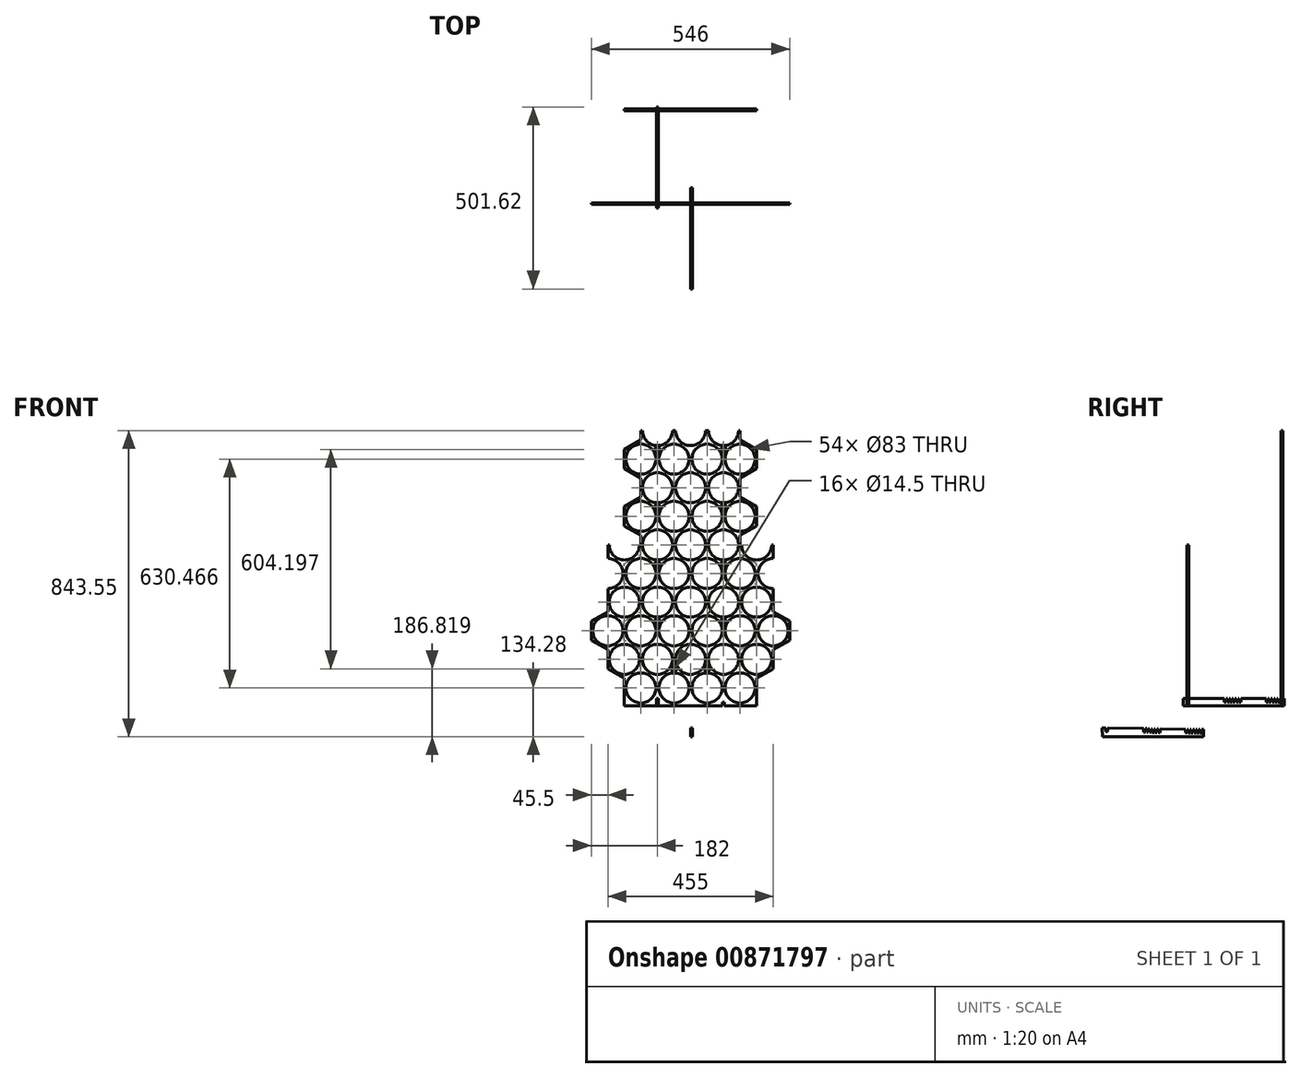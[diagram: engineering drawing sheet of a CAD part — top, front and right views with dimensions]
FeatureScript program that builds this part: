
annotation { "Feature Type Name" : "Feature", "Feature Type Description" : "" }
export const myFeature = defineFeature(function(context is Context, id is Id, definition is map)
    precondition{}
    {
        {
            var Q0;
            Q0=qCreatedBy(makeId("Front.planeOp"),FACE);
            var sketch = newSketch(context, id + "F0", { "sketchPlane" : qUnion([Q0])});
            skLineSegment(sketch, "E0", {"start": v(0, 0) * mm, "end": v(-88.5, 0) * mm});
            skCircle(sketch, "E1", {"center": v(-45.5, 49.5) * mm, "radius": 41.5 * mm});
            skCircle(sketch, "E2", {"center": v(-136.5, 49.5) * mm, "radius": 41.5 * mm});
            skCircle(sketch, "E3", {"center": v(-91, 128.3) * mm, "radius": 41.5 * mm});
            skCircle(sketch, "E4", {"center": v(-182, 128.3) * mm, "radius": 41.5 * mm});
            skArc(sketch, "E5", {"start": v(0, 169.8) * mm, "mid": v(-41.5, 128.3) * mm, "end": v(0, 86.8) * mm});
            skLineSegment(sketch, "E6.trimOffspring", {"start": v(0, 86.8) * mm, "end": v(0, 0) * mm});
            skLineSegment(sketch, "E7", {"start": v(-182, 0) * mm, "end": v(-182, 75.77) * mm});
            skLineSegment(sketch, "E8", {"start": v(-182, 75.77) * mm, "end": v(-227.5, 102.04) * mm});
            skLineSegment(sketch, "E9", {"start": v(-227.5, 102.04) * mm, "end": v(-227.5, 154.58) * mm});
            skLineSegment(sketch, "E10", {"start": v(-227.5, 154.58) * mm, "end": v(-182, 180.85) * mm});
            skLineSegment(sketch, "E11", {"start": v(-182, 180.85) * mm, "end": v(-136.5, 154.58) * mm});
            skLineSegment(sketch, "E12", {"start": v(-136.5, 154.58) * mm, "end": v(-91, 180.85) * mm});
            skLineSegment(sketch, "E13", {"start": v(-91, 180.85) * mm, "end": v(-45.5, 154.58) * mm});
            skLineSegment(sketch, "E14", {"start": v(-45.5, 154.58) * mm, "end": v(0, 180.85) * mm});
            skLineSegment(sketch, "E15", {"start": v(0, 180.85) * mm, "end": v(0, 169.8) * mm});
            skLineSegment(sketch, "E16", {"start": v(-93.5, 0) * mm, "end": v(-93.5, 10) * mm});
            skLineSegment(sketch, "E17", {"start": v(-93.5, 10) * mm, "end": v(-88.5, 10) * mm});
            skLineSegment(sketch, "E18", {"start": v(-88.5, 10) * mm, "end": v(-88.5, 0) * mm});
            skLineSegment(sketch, "E19", {"start": v(-91, 69.8) * mm, "end": v(-91, 32.96) * mm, "construction": true});
            skLineSegment(sketch, "E20.trimOffspring", {"start": v(-93.5, 0) * mm, "end": v(-182, 0) * mm});
            skSolve(sketch);
        }
        {
            var Q0;
            Q0=makeQuery(id+"F0.imprint","IMPRINT",FACE,{"disambiguationData":[TD([[makeQuery(id+"F0.imprint","IMPRINT",EDGE,{"derivedFrom":sQuery(id+"F0.wireOp",EDGE,"E0")}),-1.0]])]});
            extrude(context, id + "F1", {"entities" : qUnion([Q0]), "depth" : 5 * mm, "offsetDistance" : 25 * mm});
        }
        {
            var Q0;
            Q0=qCreatedBy(makeId("Front.planeOp"),FACE);
            var sketch = newSketch(context, id + "F2", { "sketchPlane" : qUnion([Q0])});
            skCircle(sketch, "E21", {"center": v(-136.5, 207.12) * mm, "radius": 41.5 * mm});
            skCircle(sketch, "E22", {"center": v(-45.5, 207.12) * mm, "radius": 41.5 * mm});
            skCircle(sketch, "E23", {"center": v(-227.5, 207.12) * mm, "radius": 41.5 * mm});
            skLineSegment(sketch, "E24.0", {"start": v(-45.5, 154.58) * mm, "end": v(0, 180.85) * mm});
            skLineSegment(sketch, "E24.1", {"start": v(-91, 180.85) * mm, "end": v(-45.5, 154.58) * mm});
            skLineSegment(sketch, "E24.2", {"start": v(-136.5, 154.58) * mm, "end": v(-91, 180.85) * mm});
            skLineSegment(sketch, "E24.3", {"start": v(-182, 180.85) * mm, "end": v(-136.5, 154.58) * mm});
            skLineSegment(sketch, "E24.4", {"start": v(-227.5, 154.58) * mm, "end": v(-182, 180.85) * mm});
            skLineSegment(sketch, "E25", {"start": v(-227.5, 154.58) * mm, "end": v(-273, 180.85) * mm});
            skLineSegment(sketch, "E26", {"start": v(-273, 180.85) * mm, "end": v(-273, 233.39) * mm});
            skLineSegment(sketch, "E27", {"start": v(-227.5, 312.2) * mm, "end": v(-182, 338.46) * mm});
            skLineSegment(sketch, "E28", {"start": v(-182, 338.46) * mm, "end": v(-136.5, 312.2) * mm});
            skLineSegment(sketch, "E29", {"start": v(-136.5, 312.2) * mm, "end": v(-91, 338.46) * mm});
            skLineSegment(sketch, "E30", {"start": v(-91, 338.46) * mm, "end": v(-45.5, 312.2) * mm});
            skLineSegment(sketch, "E31", {"start": v(-45.5, 312.2) * mm, "end": v(0, 338.46) * mm});
            skCircle(sketch, "E32", {"center": v(-182, 285.92) * mm, "radius": 41.5 * mm});
            skCircle(sketch, "E33", {"center": v(-91, 285.92) * mm, "radius": 41.5 * mm});
            skArc(sketch, "E34", {"start": v(0, 327.42) * mm, "mid": v(-41.5, 285.92) * mm, "end": v(0, 244.42) * mm});
            skLineSegment(sketch, "E35", {"start": v(0, 338.46) * mm, "end": v(0, 180.85) * mm});
            skLineSegment(sketch, "E36", {"start": v(-227.5, 312.2) * mm, "end": v(-227.5, 259.66) * mm});
            skLineSegment(sketch, "E37", {"start": v(-227.5, 259.66) * mm, "end": v(-273, 233.39) * mm});
            skSolve(sketch);
        }
        {
            var Q0;
            Q0=makeQuery(id+"F2.imprint","IMPRINT",FACE,{"disambiguationData":[TD([[makeQuery(id+"F2.imprint","IMPRINT",EDGE,{"derivedFrom":sQuery(id+"F2.wireOp",EDGE,"E21")}),-1.0]])]});
            extrude(context, id + "F3", {"entities" : qUnion([Q0]), "depth" : 5 * mm, "offsetDistance" : 25 * mm});
        }
        {
            var Q0;
            Q0=qCreatedBy(makeId("Front.planeOp"),FACE);
            var sketch = newSketch(context, id + "F4", { "sketchPlane" : qUnion([Q0])});
            skCircle(sketch, "E38", {"center": v(-136.5, 364.73) * mm, "radius": 41.5 * mm});
            skCircle(sketch, "E39", {"center": v(-45.5, 364.73) * mm, "radius": 41.5 * mm});
            skArc(sketch, "E40", {"start": v(-227.5, 323.23) * mm, "mid": v(-186, 364.73) * mm, "end": v(-227.5, 406.23) * mm});
            skLineSegment(sketch, "E41.0", {"start": v(-45.5, 312.2) * mm, "end": v(0, 338.46) * mm});
            skLineSegment(sketch, "E41.1", {"start": v(-91, 338.46) * mm, "end": v(-45.5, 312.2) * mm});
            skLineSegment(sketch, "E41.2", {"start": v(-136.5, 312.2) * mm, "end": v(-91, 338.46) * mm});
            skLineSegment(sketch, "E41.3", {"start": v(-182, 338.46) * mm, "end": v(-136.5, 312.2) * mm});
            skLineSegment(sketch, "E41.4", {"start": v(-227.5, 312.2) * mm, "end": v(-182, 338.46) * mm});
            skArc(sketch, "E42", {"start": v(-223.5, 443.54) * mm, "mid": v(-182, 402.04) * mm, "end": v(-140.5, 443.54) * mm});
            skArc(sketch, "E43", {"start": v(-49.5, 443.54) * mm, "mid": v(-91, 402.04) * mm, "end": v(-132.5, 443.54) * mm});
            skArc(sketch, "E44", {"start": v(-41.5, 443.54) * mm, "mid": v(-29.34, 414.2) * mm, "end": v(0, 402.04) * mm});
            skLineSegment(sketch, "E45", {"start": v(0, 402.04) * mm, "end": v(0, 338.46) * mm});
            skLineSegment(sketch, "E46", {"start": v(-41.5, 443.54) * mm, "end": v(-49.5, 443.54) * mm});
            skLineSegment(sketch, "E47", {"start": v(-227.5, 443.54) * mm, "end": v(-227.5, 406.23) * mm});
            skLineSegment(sketch, "E48.trimOffspring", {"start": v(-132.5, 443.54) * mm, "end": v(-140.5, 443.54) * mm});
            skLineSegment(sketch, "E49.trimOffspring", {"start": v(-223.5, 443.54) * mm, "end": v(-227.5, 443.54) * mm});
            skLineSegment(sketch, "E50.trimOffspring", {"start": v(-227.5, 323.23) * mm, "end": v(-227.5, 312.2) * mm});
            skSolve(sketch);
        }
        {
            var Q0;
            Q0=makeQuery(id+"F4.imprint","IMPRINT",FACE,{"disambiguationData":[TD([[makeQuery(id+"F4.imprint","IMPRINT",EDGE,{"derivedFrom":sQuery(id+"F4.wireOp",EDGE,"E38")}),-1.0]])]});
            extrude(context, id + "F5", {"entities" : qUnion([Q0]), "depth" : 5 * mm, "offsetDistance" : 25 * mm});
        }
        {
            var Q0;
            Q0=makeQuery(id+"F1.opExtrude","SWEPT_BODY",BODY,{"disambiguationData":[OSD([sQuery(id+"F0.wireOp",EDGE,"E0"),sQuery(id+"F0.wireOp",EDGE,"E1"),sQuery(id+"F0.wireOp",EDGE,"E2"),sQuery(id+"F0.wireOp",EDGE,"mhG7m76X-4i78-9KUi-kGeG-KYTDKgltDtsj"),sQuery(id+"F0.wireOp",EDGE,"E3"),sQuery(id+"F0.wireOp",EDGE,"E4"),sQuery(id+"F0.wireOp",EDGE,"E5"),sQuery(id+"F0.wireOp",EDGE,"E6.trimOffspring"),sQuery(id+"F0.wireOp",EDGE,"E7"),sQuery(id+"F0.wireOp",EDGE,"E8"),sQuery(id+"F0.wireOp",EDGE,"E9"),sQuery(id+"F0.wireOp",EDGE,"E10"),sQuery(id+"F0.wireOp",EDGE,"E11"),sQuery(id+"F0.wireOp",EDGE,"E12"),sQuery(id+"F0.wireOp",EDGE,"E13"),sQuery(id+"F0.wireOp",EDGE,"E14"),sQuery(id+"F0.wireOp",EDGE,"E15")])]});
            var Q1;
            Q1=qCreatedBy(makeId("Right.planeOp"),FACE);
            mirror(context, id + "F6", {"operationType" : NewBodyOperationType.ADD, "entities" : qUnion([Q0]), "mirrorPlane" : qUnion([Q1])});
        }
        {
            var Q0;
            Q0=makeQuery(id+"F3.opExtrude","SWEPT_BODY",BODY,{"disambiguationData":[OSD([sQuery(id+"F2.wireOp",EDGE,"E21"),sQuery(id+"F2.wireOp",EDGE,"E22"),sQuery(id+"F2.wireOp",EDGE,"E23"),sQuery(id+"F2.wireOp",EDGE,"E24.0"),sQuery(id+"F2.wireOp",EDGE,"E24.1"),sQuery(id+"F2.wireOp",EDGE,"E24.2"),sQuery(id+"F2.wireOp",EDGE,"E24.3"),sQuery(id+"F2.wireOp",EDGE,"E24.4"),sQuery(id+"F2.wireOp",EDGE,"E25"),sQuery(id+"F2.wireOp",EDGE,"E26"),sQuery(id+"F2.wireOp",EDGE,"HmdMfbAw-Pn7L-uGTa-biym-ugAkbdCf055X"),sQuery(id+"F2.wireOp",EDGE,"EBHknhmP-EQ6G-lQGi-JgQt-V6veGF6rF7o8"),sQuery(id+"F2.wireOp",EDGE,"SgolkBf5-gks9-Kuf7-9uFn-MVlt96loWBhC"),sQuery(id+"F2.wireOp",EDGE,"tphNsefZ-TArE-KIxs-TGb4-btlr9hmM9way"),sQuery(id+"F2.wireOp",EDGE,"E27"),sQuery(id+"F2.wireOp",EDGE,"E28"),sQuery(id+"F2.wireOp",EDGE,"E29"),sQuery(id+"F2.wireOp",EDGE,"E30"),sQuery(id+"F2.wireOp",EDGE,"E31"),sQuery(id+"F2.wireOp",EDGE,"wdkVYjrY-Z1xr-Qbjx-1QjL-lYbGxcBW8i4f"),sQuery(id+"F2.wireOp",EDGE,"E32"),sQuery(id+"F2.wireOp",EDGE,"E33"),sQuery(id+"F2.wireOp",EDGE,"E34"),sQuery(id+"F2.wireOp",EDGE,"E35")])]});
            var Q1;
            Q1=qCreatedBy(makeId("Right.planeOp"),FACE);
            mirror(context, id + "F7", {"operationType" : NewBodyOperationType.ADD, "entities" : qUnion([Q0]), "mirrorPlane" : qUnion([Q1])});
        }
        {
            var Q0;
            Q0=makeQuery(id+"F5.opExtrude","SWEPT_BODY",BODY,{"disambiguationData":[OSD([sQuery(id+"F4.wireOp",EDGE,"E38"),sQuery(id+"F4.wireOp",EDGE,"E39"),sQuery(id+"F4.wireOp",EDGE,"E40"),sQuery(id+"F4.wireOp",EDGE,"E41.0"),sQuery(id+"F4.wireOp",EDGE,"E41.1"),sQuery(id+"F4.wireOp",EDGE,"E41.2"),sQuery(id+"F4.wireOp",EDGE,"E41.3"),sQuery(id+"F4.wireOp",EDGE,"E41.4"),sQuery(id+"F4.wireOp",EDGE,"E42"),sQuery(id+"F4.wireOp",EDGE,"E43"),sQuery(id+"F4.wireOp",EDGE,"E44"),sQuery(id+"F4.wireOp",EDGE,"E45"),sQuery(id+"F4.wireOp",EDGE,"E46"),sQuery(id+"F4.wireOp",EDGE,"E47"),sQuery(id+"F4.wireOp",EDGE,"E48.trimOffspring"),sQuery(id+"F4.wireOp",EDGE,"E49.trimOffspring"),sQuery(id+"F4.wireOp",EDGE,"E50.trimOffspring")])]});
            var Q1;
            Q1=qCreatedBy(makeId("Right.planeOp"),FACE);
            mirror(context, id + "F8", {"operationType" : NewBodyOperationType.ADD, "entities" : qUnion([Q0]), "mirrorPlane" : qUnion([Q1])});
        }
        {
            var Q0;
            Q0=makeQuery(id+"F1.opExtrude","SWEPT_FACE",FACE,{"disambiguationData":[OSD([sQuery(id+"F0.wireOp",EDGE,"E16")])]});
            var sketch = newSketch(context, id + "F9", { "sketchPlane" : qUnion([Q0])});
            skLineSegment(sketch, "E51", {"start": v(-15, 0) * mm, "end": v(264, 0) * mm});
            skLineSegment(sketch, "E52", {"start": v(-15, 0) * mm, "end": v(-15, 20) * mm});
            skLineSegment(sketch, "E53", {"start": v(-15, 20) * mm, "end": v(-5, 20) * mm});
            skLineSegment(sketch, "E54", {"start": v(264, 20) * mm, "end": v(264, 0) * mm});
            skLineSegment(sketch, "E55", {"start": v(-5, 20) * mm, "end": v(-5, 10) * mm});
            skLineSegment(sketch, "E56", {"start": v(-5, 10) * mm, "end": v(0, 10) * mm});
            skLineSegment(sketch, "E57", {"start": v(0, 10) * mm, "end": v(0, 20) * mm});
            skLineSegment(sketch, "E58.trimOffspring", {"start": v(0, 20) * mm, "end": v(99, 20) * mm});
            skLineSegment(sketch, "E59", {"start": v(144, 20) * mm, "end": v(144, 10) * mm});
            skLineSegment(sketch, "E60", {"start": v(144, 10) * mm, "end": v(139, 10) * mm});
            skLineSegment(sketch, "E61", {"start": v(139, 10) * mm, "end": v(139, 20) * mm});
            skLineSegment(sketch, "E62.1.0.0", {"start": v(131, 10) * mm, "end": v(131, 20) * mm});
            skLineSegment(sketch, "E62.1.0.1", {"start": v(136, 10) * mm, "end": v(131, 10) * mm});
            skLineSegment(sketch, "E62.1.0.2", {"start": v(136, 20) * mm, "end": v(136, 10) * mm});
            skLineSegment(sketch, "E62.2.0.0", {"start": v(123, 10) * mm, "end": v(123, 20) * mm});
            skLineSegment(sketch, "E62.2.0.1", {"start": v(128, 10) * mm, "end": v(123, 10) * mm});
            skLineSegment(sketch, "E62.2.0.2", {"start": v(128, 20) * mm, "end": v(128, 10) * mm});
            skLineSegment(sketch, "E62.direction1", {"start": v(139, 10) * mm, "end": v(131, 10) * mm, "construction": true});
            skLineSegment(sketch, "E63.trimOffspring", {"start": v(128, 20) * mm, "end": v(131, 20) * mm});
            skLineSegment(sketch, "E64.trimOffspring", {"start": v(136, 20) * mm, "end": v(139, 20) * mm});
            skLineSegment(sketch, "E65.trimOffspring", {"start": v(144, 20) * mm, "end": v(214, 20) * mm});
            skLineSegment(sketch, "E66.0.3.0", {"start": v(115, 10) * mm, "end": v(115, 20) * mm});
            skLineSegment(sketch, "E66.3.3.0", {"start": v(120, 10) * mm, "end": v(115, 10) * mm});
            skLineSegment(sketch, "E66.6.3.0", {"start": v(120, 20) * mm, "end": v(120, 10) * mm});
            skLineSegment(sketch, "E66.0.4.0", {"start": v(107, 10) * mm, "end": v(107, 20) * mm});
            skLineSegment(sketch, "E66.3.4.0", {"start": v(112, 10) * mm, "end": v(107, 10) * mm});
            skLineSegment(sketch, "E66.6.4.0", {"start": v(112, 20) * mm, "end": v(112, 10) * mm});
            skLineSegment(sketch, "E66.0.5.0", {"start": v(99, 10) * mm, "end": v(99, 20) * mm});
            skLineSegment(sketch, "E66.3.5.0", {"start": v(104, 10) * mm, "end": v(99, 10) * mm});
            skLineSegment(sketch, "E66.6.5.0", {"start": v(104, 20) * mm, "end": v(104, 10) * mm});
            skLineSegment(sketch, "E67.trimOffspring", {"start": v(104, 20) * mm, "end": v(107, 20) * mm});
            skLineSegment(sketch, "E68.trimOffspring", {"start": v(112, 20) * mm, "end": v(115, 20) * mm});
            skLineSegment(sketch, "E69.trimOffspring", {"start": v(120, 20) * mm, "end": v(123, 20) * mm});
            skLineSegment(sketch, "E70.1.0.0", {"start": v(219, 10) * mm, "end": v(214, 10) * mm});
            skLineSegment(sketch, "E70.1.0.1", {"start": v(259, 20) * mm, "end": v(259, 10) * mm});
            skLineSegment(sketch, "E70.1.0.2", {"start": v(214, 10) * mm, "end": v(214, 20) * mm});
            skLineSegment(sketch, "E70.1.0.3", {"start": v(243, 20) * mm, "end": v(243, 10) * mm});
            skLineSegment(sketch, "E70.1.0.4", {"start": v(251, 20) * mm, "end": v(251, 10) * mm});
            skLineSegment(sketch, "E70.1.0.5", {"start": v(227, 20) * mm, "end": v(227, 10) * mm});
            skLineSegment(sketch, "E70.1.0.6", {"start": v(254, 10) * mm, "end": v(254, 20) * mm});
            skLineSegment(sketch, "E70.1.0.7", {"start": v(238, 10) * mm, "end": v(238, 20) * mm});
            skLineSegment(sketch, "E70.1.0.8", {"start": v(227, 10) * mm, "end": v(222, 10) * mm});
            skLineSegment(sketch, "E70.1.0.9", {"start": v(246, 10) * mm, "end": v(246, 20) * mm});
            skLineSegment(sketch, "E70.1.0.10", {"start": v(230, 10) * mm, "end": v(230, 20) * mm});
            skLineSegment(sketch, "E70.1.0.11", {"start": v(259, 10) * mm, "end": v(254, 10) * mm});
            skLineSegment(sketch, "E70.1.0.12", {"start": v(235, 10) * mm, "end": v(230, 10) * mm});
            skLineSegment(sketch, "E70.1.0.13", {"start": v(235, 20) * mm, "end": v(235, 10) * mm});
            skLineSegment(sketch, "E70.1.0.14", {"start": v(219, 20) * mm, "end": v(219, 10) * mm});
            skLineSegment(sketch, "E70.1.0.15", {"start": v(243, 10) * mm, "end": v(238, 10) * mm});
            skLineSegment(sketch, "E70.1.0.16", {"start": v(222, 10) * mm, "end": v(222, 20) * mm});
            skLineSegment(sketch, "E70.1.0.17", {"start": v(251, 10) * mm, "end": v(246, 10) * mm});
            skLineSegment(sketch, "E70.direction1", {"start": v(99, 10) * mm, "end": v(214, 10) * mm, "construction": true});
            skLineSegment(sketch, "E71.trimOffspring", {"start": v(219, 20) * mm, "end": v(222, 20) * mm});
            skLineSegment(sketch, "E72.trimOffspring", {"start": v(227, 20) * mm, "end": v(230, 20) * mm});
            skLineSegment(sketch, "E73.trimOffspring", {"start": v(235, 20) * mm, "end": v(238, 20) * mm});
            skLineSegment(sketch, "E74.trimOffspring", {"start": v(243, 20) * mm, "end": v(246, 20) * mm});
            skLineSegment(sketch, "E75.trimOffspring", {"start": v(251, 20) * mm, "end": v(254, 20) * mm});
            skLineSegment(sketch, "E76.trimOffspring", {"start": v(259, 20) * mm, "end": v(264, 20) * mm});
            skSolve(sketch);
        }
        {
            var Q0;
            Q0 = qSketchRegion(id + "F9", true);
            extrude(context, id + "F10", {"entities" : qUnion([Q0]), "depth" : 5 * mm, "offsetDistance" : 25 * mm});
        }
        {
            var Q0;
            Q0=makeQuery(id+"F10.opExtrude","SWEPT_FACE",FACE,{"disambiguationData":[OSD([sQuery(id+"F9.wireOp",EDGE,"E70.1.0.1")])]});
            var sketch = newSketch(context, id + "F11", { "sketchPlane" : qUnion([Q0])});
            skCircle(sketch, "E77.0", {"center": v(-45.5, 49.5) * mm, "radius": 41.5 * mm});
            skCircle(sketch, "E77.1", {"center": v(45.5, 49.5) * mm, "radius": 41.5 * mm});
            skCircle(sketch, "E77.2", {"center": v(0, 128.3) * mm, "radius": 41.5 * mm});
            skCircle(sketch, "E78.0.1.0", {"center": v(45.5, 207.12) * mm, "radius": 41.5 * mm});
            skCircle(sketch, "E78.0.1.1", {"center": v(0, 285.92) * mm, "radius": 41.5 * mm});
            skCircle(sketch, "E78.0.1.2", {"center": v(-45.5, 207.12) * mm, "radius": 41.5 * mm});
            skCircle(sketch, "E78.0.2.0", {"center": v(45.5, 364.73) * mm, "radius": 41.5 * mm});
            skCircle(sketch, "E78.0.2.1", {"center": v(0, 443.54) * mm, "radius": 41.5 * mm});
            skCircle(sketch, "E78.0.2.2", {"center": v(-45.5, 364.73) * mm, "radius": 41.5 * mm});
            skLineSegment(sketch, "E78.direction1", {"start": v(-45.5, 49.5) * mm, "end": v(-20.5, 49.5) * mm, "construction": true});
            skLineSegment(sketch, "E78.direction2", {"start": v(-45.5, 49.5) * mm, "end": v(-45.5, 207.12) * mm, "construction": true});
            skCircle(sketch, "E79.0.0.3", {"center": v(45.5, 522.35) * mm, "radius": 41.5 * mm});
            skCircle(sketch, "E79.2.0.3", {"center": v(0, 601.16) * mm, "radius": 41.5 * mm});
            skCircle(sketch, "E79.4.0.3", {"center": v(-45.5, 522.35) * mm, "radius": 41.5 * mm});
            skLineSegment(sketch, "E80.0", {"start": v(88.5, 0) * mm, "end": v(-88.5, 0) * mm});
            skLineSegment(sketch, "E81", {"start": v(-88.5, 0) * mm, "end": v(-88.5, 10) * mm});
            skLineSegment(sketch, "E82", {"start": v(-88.5, 10) * mm, "end": v(-93.5, 10) * mm});
            skLineSegment(sketch, "E83", {"start": v(-93.5, 10) * mm, "end": v(-93.5, 0) * mm});
            skLineSegment(sketch, "E84", {"start": v(-93.5, 0) * mm, "end": v(-136.5, 0) * mm});
            skLineSegment(sketch, "E85", {"start": v(0, 12.29) * mm, "end": v(0, -20.5) * mm, "construction": true});
            skCircle(sketch, "E86.0", {"center": v(91, 128.3) * mm, "radius": 41.5 * mm});
            skCircle(sketch, "E86.1", {"center": v(-91, 128.3) * mm, "radius": 41.5 * mm});
            skCircle(sketch, "E86.2", {"center": v(-91, 285.92) * mm, "radius": 41.5 * mm});
            skCircle(sketch, "E86.3", {"center": v(91, 285.92) * mm, "radius": 41.5 * mm});
            skCircle(sketch, "E87", {"center": v(91, 443.54) * mm, "radius": 41.5 * mm});
            skCircle(sketch, "E88", {"center": v(-91, 443.54) * mm, "radius": 41.5 * mm});
            skCircle(sketch, "E89", {"center": v(-91, 601.16) * mm, "radius": 41.5 * mm});
            skCircle(sketch, "E90", {"center": v(91, 601.16) * mm, "radius": 41.5 * mm});
            skLineSegment(sketch, "E91.MirrorCS", {"start": v(93.5, 0) * mm, "end": v(136.5, 0) * mm});
            skLineSegment(sketch, "E92.MirrorCS", {"start": v(93.5, 10) * mm, "end": v(93.5, 0) * mm});
            skLineSegment(sketch, "E93.MirrorCS", {"start": v(88.5, 0) * mm, "end": v(88.5, 10) * mm});
            skLineSegment(sketch, "E94.MirrorCS", {"start": v(88.5, 10) * mm, "end": v(93.5, 10) * mm});
            skArc(sketch, "E95.0", {"start": v(-136.5, 8) * mm, "mid": v(-95, 49.5) * mm, "end": v(-136.5, 91) * mm});
            skArc(sketch, "E95.1", {"start": v(136.5, 91) * mm, "mid": v(95, 49.5) * mm, "end": v(136.5, 8) * mm});
            skCircle(sketch, "E96.0", {"center": v(-136.5, 207.12) * mm, "radius": 41.5 * mm});
            skCircle(sketch, "E96.1", {"center": v(136.5, 207.12) * mm, "radius": 41.5 * mm});
            skCircle(sketch, "E97", {"center": v(-136.5, 364.73) * mm, "radius": 41.5 * mm});
            skCircle(sketch, "E98", {"center": v(136.5, 364.73) * mm, "radius": 41.5 * mm});
            skCircle(sketch, "E99", {"center": v(136.5, 522.35) * mm, "radius": 41.5 * mm});
            skCircle(sketch, "E100", {"center": v(-136.5, 522.35) * mm, "radius": 41.5 * mm});
            skCircle(sketch, "E101", {"center": v(-136.5, 679.97) * mm, "radius": 41.5 * mm});
            skCircle(sketch, "E102", {"center": v(-45.5, 679.97) * mm, "radius": 41.5 * mm});
            skCircle(sketch, "E103", {"center": v(45.5, 679.97) * mm, "radius": 41.5 * mm});
            skCircle(sketch, "E104", {"center": v(136.5, 679.97) * mm, "radius": 41.5 * mm});
            skArc(sketch, "E105", {"start": v(-132.5, 758.77) * mm, "mid": v(-91, 717.27) * mm, "end": v(-49.5, 758.77) * mm});
            skArc(sketch, "E106", {"start": v(-41.5, 758.77) * mm, "mid": v(0, 717.27) * mm, "end": v(41.5, 758.77) * mm});
            skArc(sketch, "E107", {"start": v(49.5, 758.77) * mm, "mid": v(91, 717.27) * mm, "end": v(132.5, 758.77) * mm});
            skLineSegment(sketch, "E108", {"start": v(-136.5, 758.77) * mm, "end": v(-132.5, 758.77) * mm});
            skLineSegment(sketch, "E109", {"start": v(-136.5, 0) * mm, "end": v(-136.5, 8) * mm});
            skLineSegment(sketch, "E110", {"start": v(-136.5, 154.58) * mm, "end": v(-182, 180.85) * mm});
            skLineSegment(sketch, "E111", {"start": v(-182, 180.85) * mm, "end": v(-182, 233.39) * mm});
            skLineSegment(sketch, "E112", {"start": v(-182, 233.39) * mm, "end": v(-136.5, 259.66) * mm});
            skLineSegment(sketch, "E113", {"start": v(-136.5, 259.66) * mm, "end": v(-136.5, 312.2) * mm});
            skLineSegment(sketch, "E114", {"start": v(-136.5, 312.2) * mm, "end": v(-182, 338.46) * mm});
            skLineSegment(sketch, "E115", {"start": v(-182, 338.46) * mm, "end": v(-182, 391) * mm});
            skLineSegment(sketch, "E116", {"start": v(-182, 391) * mm, "end": v(-136.5, 417.27) * mm});
            skLineSegment(sketch, "E117", {"start": v(-136.5, 417.27) * mm, "end": v(-136.5, 469.81) * mm});
            skLineSegment(sketch, "E118", {"start": v(-136.5, 469.81) * mm, "end": v(-182, 496.08) * mm});
            skLineSegment(sketch, "E119", {"start": v(-182, 496.08) * mm, "end": v(-182, 548.62) * mm});
            skLineSegment(sketch, "E120", {"start": v(-182, 548.62) * mm, "end": v(-136.5, 574.89) * mm});
            skLineSegment(sketch, "E121", {"start": v(-136.5, 574.89) * mm, "end": v(-136.5, 627.43) * mm});
            skLineSegment(sketch, "E122", {"start": v(-136.5, 627.43) * mm, "end": v(-182, 653.7) * mm});
            skLineSegment(sketch, "E123", {"start": v(-182, 653.7) * mm, "end": v(-182, 706.24) * mm});
            skLineSegment(sketch, "E124", {"start": v(-182, 706.24) * mm, "end": v(-136.5, 732.5) * mm});
            skLineSegment(sketch, "E125", {"start": v(-136.5, 732.5) * mm, "end": v(-136.5, 758.77) * mm});
            skLineSegment(sketch, "E126.MirrorCS", {"start": v(136.5, 0) * mm, "end": v(136.5, 8) * mm});
            skLineSegment(sketch, "E127.MirrorCS", {"start": v(136.5, 154.58) * mm, "end": v(182, 180.85) * mm});
            skLineSegment(sketch, "E128.MirrorCS", {"start": v(182, 180.85) * mm, "end": v(182, 233.39) * mm});
            skLineSegment(sketch, "E129.MirrorCS", {"start": v(182, 233.39) * mm, "end": v(136.5, 259.66) * mm});
            skLineSegment(sketch, "E130.MirrorCS", {"start": v(136.5, 259.66) * mm, "end": v(136.5, 312.2) * mm});
            skLineSegment(sketch, "E131.MirrorCS", {"start": v(136.5, 312.2) * mm, "end": v(182, 338.46) * mm});
            skLineSegment(sketch, "E132.MirrorCS", {"start": v(182, 338.46) * mm, "end": v(182, 391) * mm});
            skLineSegment(sketch, "E133.MirrorCS", {"start": v(182, 391) * mm, "end": v(136.5, 417.27) * mm});
            skLineSegment(sketch, "E134.MirrorCS", {"start": v(136.5, 417.27) * mm, "end": v(136.5, 469.81) * mm});
            skLineSegment(sketch, "E135.MirrorCS", {"start": v(136.5, 469.81) * mm, "end": v(182, 496.08) * mm});
            skLineSegment(sketch, "E136.MirrorCS", {"start": v(182, 496.08) * mm, "end": v(182, 548.62) * mm});
            skLineSegment(sketch, "E137.MirrorCS", {"start": v(182, 548.62) * mm, "end": v(136.5, 574.89) * mm});
            skLineSegment(sketch, "E138.MirrorCS", {"start": v(136.5, 574.89) * mm, "end": v(136.5, 627.43) * mm});
            skLineSegment(sketch, "E139.MirrorCS", {"start": v(136.5, 627.43) * mm, "end": v(182, 653.7) * mm});
            skLineSegment(sketch, "E140.MirrorCS", {"start": v(182, 653.7) * mm, "end": v(182, 706.24) * mm});
            skLineSegment(sketch, "E141.MirrorCS", {"start": v(182, 706.24) * mm, "end": v(136.5, 732.5) * mm});
            skLineSegment(sketch, "E142.MirrorCS", {"start": v(136.5, 732.5) * mm, "end": v(136.5, 758.77) * mm});
            skLineSegment(sketch, "E143.trimOffspring", {"start": v(132.5, 758.77) * mm, "end": v(136.5, 758.77) * mm});
            skLineSegment(sketch, "E144.trimOffspring", {"start": v(41.5, 758.77) * mm, "end": v(49.5, 758.77) * mm});
            skLineSegment(sketch, "E145.trimOffspring", {"start": v(-49.5, 758.77) * mm, "end": v(-41.5, 758.77) * mm});
            skLineSegment(sketch, "E146.trimOffspring", {"start": v(-136.5, 91) * mm, "end": v(-136.5, 154.58) * mm});
            skLineSegment(sketch, "E147.trimOffspring", {"start": v(136.5, 91) * mm, "end": v(136.5, 154.58) * mm});
            skSolve(sketch);
        }
        {
            var Q0;
            Q0 = qSketchRegion(id + "F11", true);
            extrude(context, id + "F12", {"entities" : qUnion([Q0]), "depth" : 5 * mm, "offsetDistance" : 25 * mm});
        }
        {
            var Q0;
            Q0=makeQuery(id+"F12.opExtrude","CAP_FACE",FACE,{"disambiguationData":[OSD([sQuery(id+"F11.wireOp",EDGE,"E77.0"),sQuery(id+"F11.wireOp",EDGE,"E77.1"),sQuery(id+"F11.wireOp",EDGE,"E77.2"),sQuery(id+"F11.wireOp",EDGE,"E78.0.1.0"),sQuery(id+"F11.wireOp",EDGE,"E78.0.1.1"),sQuery(id+"F11.wireOp",EDGE,"E78.0.1.2"),sQuery(id+"F11.wireOp",EDGE,"E78.0.2.0"),sQuery(id+"F11.wireOp",EDGE,"E78.0.2.1"),sQuery(id+"F11.wireOp",EDGE,"E78.0.2.2"),sQuery(id+"F11.wireOp",EDGE,"E79.0.0.3"),sQuery(id+"F11.wireOp",EDGE,"E79.2.0.3"),sQuery(id+"F11.wireOp",EDGE,"E79.4.0.3"),sQuery(id+"F11.wireOp",EDGE,"E80.0"),sQuery(id+"F11.wireOp",EDGE,"E81"),sQuery(id+"F11.wireOp",EDGE,"E82"),sQuery(id+"F11.wireOp",EDGE,"E83"),sQuery(id+"F11.wireOp",EDGE,"E84"),sQuery(id+"F11.wireOp",EDGE,"E86.0"),sQuery(id+"F11.wireOp",EDGE,"E86.1"),sQuery(id+"F11.wireOp",EDGE,"E86.2"),sQuery(id+"F11.wireOp",EDGE,"E86.3"),sQuery(id+"F11.wireOp",EDGE,"E87"),sQuery(id+"F11.wireOp",EDGE,"E88"),sQuery(id+"F11.wireOp",EDGE,"E89"),sQuery(id+"F11.wireOp",EDGE,"E90"),sQuery(id+"F11.wireOp",EDGE,"E91.MirrorCS"),sQuery(id+"F11.wireOp",EDGE,"E92.MirrorCS"),sQuery(id+"F11.wireOp",EDGE,"E93.MirrorCS"),sQuery(id+"F11.wireOp",EDGE,"E94.MirrorCS"),sQuery(id+"F11.wireOp",EDGE,"E95.0"),sQuery(id+"F11.wireOp",EDGE,"E95.1"),sQuery(id+"F11.wireOp",EDGE,"E96.0"),sQuery(id+"F11.wireOp",EDGE,"E96.1"),sQuery(id+"F11.wireOp",EDGE,"E97"),sQuery(id+"F11.wireOp",EDGE,"E98"),sQuery(id+"F11.wireOp",EDGE,"E99"),sQuery(id+"F11.wireOp",EDGE,"E100"),sQuery(id+"F11.wireOp",EDGE,"E101"),sQuery(id+"F11.wireOp",EDGE,"E102"),sQuery(id+"F11.wireOp",EDGE,"E103"),sQuery(id+"F11.wireOp",EDGE,"E104"),sQuery(id+"F11.wireOp",EDGE,"E105"),sQuery(id+"F11.wireOp",EDGE,"E106"),sQuery(id+"F11.wireOp",EDGE,"E107"),sQuery(id+"F11.wireOp",EDGE,"E108"),sQuery(id+"F11.wireOp",EDGE,"E109"),sQuery(id+"F11.wireOp",EDGE,"E110"),sQuery(id+"F11.wireOp",EDGE,"E111"),sQuery(id+"F11.wireOp",EDGE,"E112"),sQuery(id+"F11.wireOp",EDGE,"E113"),sQuery(id+"F11.wireOp",EDGE,"E114"),sQuery(id+"F11.wireOp",EDGE,"E115"),sQuery(id+"F11.wireOp",EDGE,"E116"),sQuery(id+"F11.wireOp",EDGE,"E117"),sQuery(id+"F11.wireOp",EDGE,"E118"),sQuery(id+"F11.wireOp",EDGE,"E119"),sQuery(id+"F11.wireOp",EDGE,"E120"),sQuery(id+"F11.wireOp",EDGE,"E121"),sQuery(id+"F11.wireOp",EDGE,"E122"),sQuery(id+"F11.wireOp",EDGE,"E123"),sQuery(id+"F11.wireOp",EDGE,"E124"),sQuery(id+"F11.wireOp",EDGE,"E125"),sQuery(id+"F11.wireOp",EDGE,"E126.MirrorCS"),sQuery(id+"F11.wireOp",EDGE,"E127.MirrorCS"),sQuery(id+"F11.wireOp",EDGE,"E128.MirrorCS"),sQuery(id+"F11.wireOp",EDGE,"E129.MirrorCS"),sQuery(id+"F11.wireOp",EDGE,"E130.MirrorCS"),sQuery(id+"F11.wireOp",EDGE,"E131.MirrorCS"),sQuery(id+"F11.wireOp",EDGE,"E132.MirrorCS"),sQuery(id+"F11.wireOp",EDGE,"E133.MirrorCS"),sQuery(id+"F11.wireOp",EDGE,"E134.MirrorCS"),sQuery(id+"F11.wireOp",EDGE,"E135.MirrorCS"),sQuery(id+"F11.wireOp",EDGE,"E136.MirrorCS"),sQuery(id+"F11.wireOp",EDGE,"E137.MirrorCS"),sQuery(id+"F11.wireOp",EDGE,"E138.MirrorCS"),sQuery(id+"F11.wireOp",EDGE,"E139.MirrorCS"),sQuery(id+"F11.wireOp",EDGE,"E140.MirrorCS"),sQuery(id+"F11.wireOp",EDGE,"E141.MirrorCS"),sQuery(id+"F11.wireOp",EDGE,"E142.MirrorCS"),sQuery(id+"F11.wireOp",EDGE,"E143.trimOffspring"),sQuery(id+"F11.wireOp",EDGE,"E144.trimOffspring"),sQuery(id+"F11.wireOp",EDGE,"E145.trimOffspring"),sQuery(id+"F11.wireOp",EDGE,"E146.trimOffspring"),sQuery(id+"F11.wireOp",EDGE,"E147.trimOffspring")])],"isStart":false});
            var sketch = newSketch(context, id + "F13", { "sketchPlane" : qUnion([Q0])});
            skCircle(sketch, "E148", {"center": v(-45.5, 102.04) * mm, "radius": 7.25 * mm});
            skCircle(sketch, "E149", {"center": v(45.5, 102.04) * mm, "radius": 7.25 * mm});
            skCircle(sketch, "E150", {"center": v(-91, 233.39) * mm, "radius": 7.25 * mm});
            skCircle(sketch, "E151", {"center": v(91, 233.39) * mm, "radius": 7.25 * mm});
            skCircle(sketch, "E152", {"center": v(-91, 391) * mm, "radius": 7.25 * mm});
            skCircle(sketch, "E153", {"center": v(91, 391) * mm, "radius": 7.25 * mm});
            skLineSegment(sketch, "E154", {"start": v(-91, 391) * mm, "end": v(-72.18, 380.14) * mm, "construction": true});
            skLineSegment(sketch, "E155", {"start": v(91, 391) * mm, "end": v(94.13, 389.2) * mm, "construction": true});
            skLineSegment(sketch, "E156", {"start": v(-111.88, 245.44) * mm, "end": v(-91, 233.39) * mm, "construction": true});
            skLineSegment(sketch, "E157", {"start": v(-11.37, 292.49) * mm, "end": v(91, 233.39) * mm, "construction": true});
            skLineSegment(sketch, "E158", {"start": v(-45.5, 266.4) * mm, "end": v(-45.5, 102.04) * mm, "construction": true});
            skLineSegment(sketch, "E159", {"start": v(-108.57, 138.45) * mm, "end": v(-45.5, 102.04) * mm, "construction": true});
            skLineSegment(sketch, "E160", {"start": v(45.5, 266.8) * mm, "end": v(45.5, 102.04) * mm, "construction": true});
            skLineSegment(sketch, "E161", {"start": v(-12.64, 135.6) * mm, "end": v(45.5, 102.04) * mm, "construction": true});
            skLineSegment(sketch, "E162", {"start": v(-62.12, 531.94) * mm, "end": v(-28.58, 512.58) * mm, "construction": true});
            skLineSegment(sketch, "E163", {"start": v(62.96, 564.8) * mm, "end": v(110.3, 537.48) * mm, "construction": true});
            skCircle(sketch, "E164", {"center": v(-91, 548.62) * mm, "radius": 7.25 * mm});
            skCircle(sketch, "E165", {"center": v(91, 548.62) * mm, "radius": 7.25 * mm});
            skCircle(sketch, "E166", {"center": v(-91, 706.24) * mm, "radius": 7.25 * mm});
            skCircle(sketch, "E167", {"center": v(91, 706.24) * mm, "radius": 7.25 * mm});
            skLineSegment(sketch, "E168", {"start": v(-91, 706.24) * mm, "end": v(-80.07, 712.55) * mm, "construction": true});
            skLineSegment(sketch, "E169", {"start": v(43.52, 678.82) * mm, "end": v(91, 706.24) * mm, "construction": true});
            skLineSegment(sketch, "E170", {"start": v(-91, 706.24) * mm, "end": v(-91, 568.78) * mm, "construction": true});
            skSolve(sketch);
        }
        {
            var Q0;
            Q0 = qSketchRegion(id + "F13", true);
            extrude(context, id + "F14", {"entities" : qUnion([Q0]), "operationType" : NewBodyOperationType.REMOVE, "endBound" : BoundingType.THROUGH_ALL, "oppositeDirection" : true, "depth" : 25 * mm, "offsetDistance" : 25 * mm, "hasSecondDirection" : true, "secondDirectionBound" : BoundingType.THROUGH_ALL, "secondDirectionOppositeDirection" : false, "secondDirectionDepth" : 25 * mm});
        }
        {
            var Q0;
            Q0=qCreatedBy(makeId("Right.planeOp"),FACE);
            var sketch = newSketch(context, id + "F15", { "sketchPlane" : qUnion([Q0])});
            skLineSegment(sketch, "E171.0.0", {"start": v(-227.62, -61.08) * mm, "end": v(-227.62, -71.08) * mm});
            skLineSegment(sketch, "E171.0.1", {"start": v(-227.62, -71.08) * mm, "end": v(-222.62, -71.15) * mm});
            skLineSegment(sketch, "E171.0.2", {"start": v(-222.62, -71.15) * mm, "end": v(-222.62, -61.15) * mm});
            skLineSegment(sketch, "E171.0.3", {"start": v(-222.62, -61.15) * mm, "end": v(-123.62, -62.5) * mm});
            skLineSegment(sketch, "E171.0.4", {"start": v(-123.62, -62.5) * mm, "end": v(-123.62, -72.5) * mm});
            skLineSegment(sketch, "E171.0.5", {"start": v(-123.62, -72.5) * mm, "end": v(-118.62, -72.58) * mm});
            skLineSegment(sketch, "E171.0.6", {"start": v(-118.62, -72.58) * mm, "end": v(-118.62, -62.58) * mm});
            skLineSegment(sketch, "E171.0.7", {"start": v(-118.62, -62.58) * mm, "end": v(-115.62, -62.62) * mm});
            skLineSegment(sketch, "E171.0.8", {"start": v(-115.62, -62.62) * mm, "end": v(-115.62, -72.62) * mm});
            skLineSegment(sketch, "E171.0.9", {"start": v(-115.62, -72.62) * mm, "end": v(-110.62, -72.69) * mm});
            skLineSegment(sketch, "E171.0.10", {"start": v(-110.62, -72.69) * mm, "end": v(-110.62, -62.69) * mm});
            skLineSegment(sketch, "E171.0.11", {"start": v(-110.62, -62.69) * mm, "end": v(-107.62, -62.73) * mm});
            skLineSegment(sketch, "E171.0.12", {"start": v(-107.62, -62.73) * mm, "end": v(-107.62, -72.73) * mm});
            skLineSegment(sketch, "E171.0.13", {"start": v(-107.62, -72.73) * mm, "end": v(-102.62, -72.8) * mm});
            skLineSegment(sketch, "E171.0.14", {"start": v(-102.62, -72.8) * mm, "end": v(-102.62, -62.8) * mm});
            skLineSegment(sketch, "E171.0.15", {"start": v(-102.62, -62.8) * mm, "end": v(-99.62, -62.84) * mm});
            skLineSegment(sketch, "E171.0.16", {"start": v(-99.62, -62.84) * mm, "end": v(-99.62, -72.84) * mm});
            skLineSegment(sketch, "E171.0.17", {"start": v(-99.62, -72.84) * mm, "end": v(-94.62, -72.9) * mm});
            skLineSegment(sketch, "E171.0.18", {"start": v(-94.62, -72.9) * mm, "end": v(-94.62, -62.9) * mm});
            skLineSegment(sketch, "E171.0.19", {"start": v(-94.62, -62.9) * mm, "end": v(-91.62, -62.95) * mm});
            skLineSegment(sketch, "E171.0.20", {"start": v(-91.62, -62.95) * mm, "end": v(-91.62, -72.95) * mm});
            skLineSegment(sketch, "E171.0.21", {"start": v(-91.62, -72.95) * mm, "end": v(-86.62, -73.02) * mm});
            skLineSegment(sketch, "E171.0.22", {"start": v(-86.62, -73.02) * mm, "end": v(-86.62, -63.02) * mm});
            skLineSegment(sketch, "E171.0.23", {"start": v(-86.62, -63.02) * mm, "end": v(-83.62, -63.06) * mm});
            skLineSegment(sketch, "E171.0.24", {"start": v(-83.62, -63.06) * mm, "end": v(-83.62, -73.06) * mm});
            skLineSegment(sketch, "E171.0.25", {"start": v(-83.62, -73.06) * mm, "end": v(-78.62, -73.13) * mm});
            skLineSegment(sketch, "E171.0.26", {"start": v(-78.62, -73.13) * mm, "end": v(-78.62, -63.13) * mm});
            skLineSegment(sketch, "E171.0.27", {"start": v(-78.62, -63.13) * mm, "end": v(-8.62, -64.09) * mm});
            skLineSegment(sketch, "E171.0.28", {"start": v(-8.62, -64.09) * mm, "end": v(-8.62, -74.09) * mm});
            skLineSegment(sketch, "E171.0.29", {"start": v(-8.62, -74.09) * mm, "end": v(-3.62, -74.16) * mm});
            skLineSegment(sketch, "E171.0.30", {"start": v(-3.62, -74.16) * mm, "end": v(-3.62, -64.16) * mm});
            skLineSegment(sketch, "E171.0.31", {"start": v(-3.62, -64.16) * mm, "end": v(-0.62, -64.2) * mm});
            skLineSegment(sketch, "E171.0.32", {"start": v(-0.62, -64.2) * mm, "end": v(-0.62, -74.2) * mm});
            skLineSegment(sketch, "E171.0.33", {"start": v(-0.62, -74.2) * mm, "end": v(4.38, -74.27) * mm});
            skLineSegment(sketch, "E171.0.34", {"start": v(4.38, -74.27) * mm, "end": v(4.38, -64.27) * mm});
            skLineSegment(sketch, "E171.0.35", {"start": v(4.38, -64.27) * mm, "end": v(7.38, -64.3) * mm});
            skLineSegment(sketch, "E171.0.36", {"start": v(7.38, -64.3) * mm, "end": v(7.38, -74.3) * mm});
            skLineSegment(sketch, "E171.0.37", {"start": v(7.38, -74.3) * mm, "end": v(12.38, -74.37) * mm});
            skLineSegment(sketch, "E171.0.38", {"start": v(12.38, -74.37) * mm, "end": v(12.38, -64.37) * mm});
            skLineSegment(sketch, "E171.0.39", {"start": v(12.38, -64.37) * mm, "end": v(15.38, -64.42) * mm});
            skLineSegment(sketch, "E171.0.40", {"start": v(15.38, -64.42) * mm, "end": v(15.38, -74.42) * mm});
            skLineSegment(sketch, "E171.0.41", {"start": v(15.38, -74.42) * mm, "end": v(20.38, -74.48) * mm});
            skLineSegment(sketch, "E171.0.42", {"start": v(20.38, -74.48) * mm, "end": v(20.38, -64.48) * mm});
            skLineSegment(sketch, "E171.0.43", {"start": v(20.38, -64.48) * mm, "end": v(23.38, -64.53) * mm});
            skLineSegment(sketch, "E171.0.44", {"start": v(23.38, -64.53) * mm, "end": v(23.38, -74.53) * mm});
            skLineSegment(sketch, "E171.0.45", {"start": v(23.38, -74.53) * mm, "end": v(28.38, -74.6) * mm});
            skLineSegment(sketch, "E171.0.46", {"start": v(28.38, -74.6) * mm, "end": v(28.38, -64.6) * mm});
            skLineSegment(sketch, "E171.0.47", {"start": v(28.38, -64.6) * mm, "end": v(31.38, -64.64) * mm});
            skLineSegment(sketch, "E171.0.48", {"start": v(31.38, -64.64) * mm, "end": v(31.38, -74.64) * mm});
            skLineSegment(sketch, "E171.0.49", {"start": v(31.38, -74.64) * mm, "end": v(36.38, -74.7) * mm});
            skLineSegment(sketch, "E171.0.50", {"start": v(36.38, -74.7) * mm, "end": v(36.38, -64.7) * mm});
            skLineSegment(sketch, "E171.0.51", {"start": v(36.38, -64.7) * mm, "end": v(41.38, -64.77) * mm});
            skLineSegment(sketch, "E171.0.52", {"start": v(41.38, -64.77) * mm, "end": v(41.38, -84.78) * mm});
            skLineSegment(sketch, "E171.0.53", {"start": v(41.38, -84.78) * mm, "end": v(-237.47, -75.04) * mm});
            skLineSegment(sketch, "E171.0.54", {"start": v(-237.47, -75.04) * mm, "end": v(-237.62, -60.95) * mm});
            skLineSegment(sketch, "E171.0.55", {"start": v(-237.62, -60.95) * mm, "end": v(-227.62, -61.08) * mm});
            skLineSegment(sketch, "E172", {"start": v(41.38, -84.78) * mm, "end": v(-237.37, -84.78) * mm});
            skLineSegment(sketch, "E173", {"start": v(-237.37, -84.78) * mm, "end": v(-237.47, -75.04) * mm});
            skSolve(sketch);
        }
        {
            var Q0;
            Q0=makeQuery(id+"F15.imprint","IMPRINT",FACE,{"disambiguationData":[TD([[makeQuery(id+"F15.imprint","IMPRINT",EDGE,{"derivedFrom":sQuery(id+"F15.wireOp",EDGE,"E171.0.0")}),-1.0]])]});
            var Q1;
            Q1=makeQuery(id+"F15.imprint","IMPRINT",FACE,{"disambiguationData":[TD([[makeQuery(id+"F15.imprint","IMPRINT",EDGE,{"derivedFrom":sQuery(id+"F15.wireOp",EDGE,"E171.0.53")}),1.0]])]});
            extrude(context, id + "F16", {"entities" : qUnion([Q0, Q1]), "depth" : 5 * mm, "offsetDistance" : 25 * mm});
        }
    });
